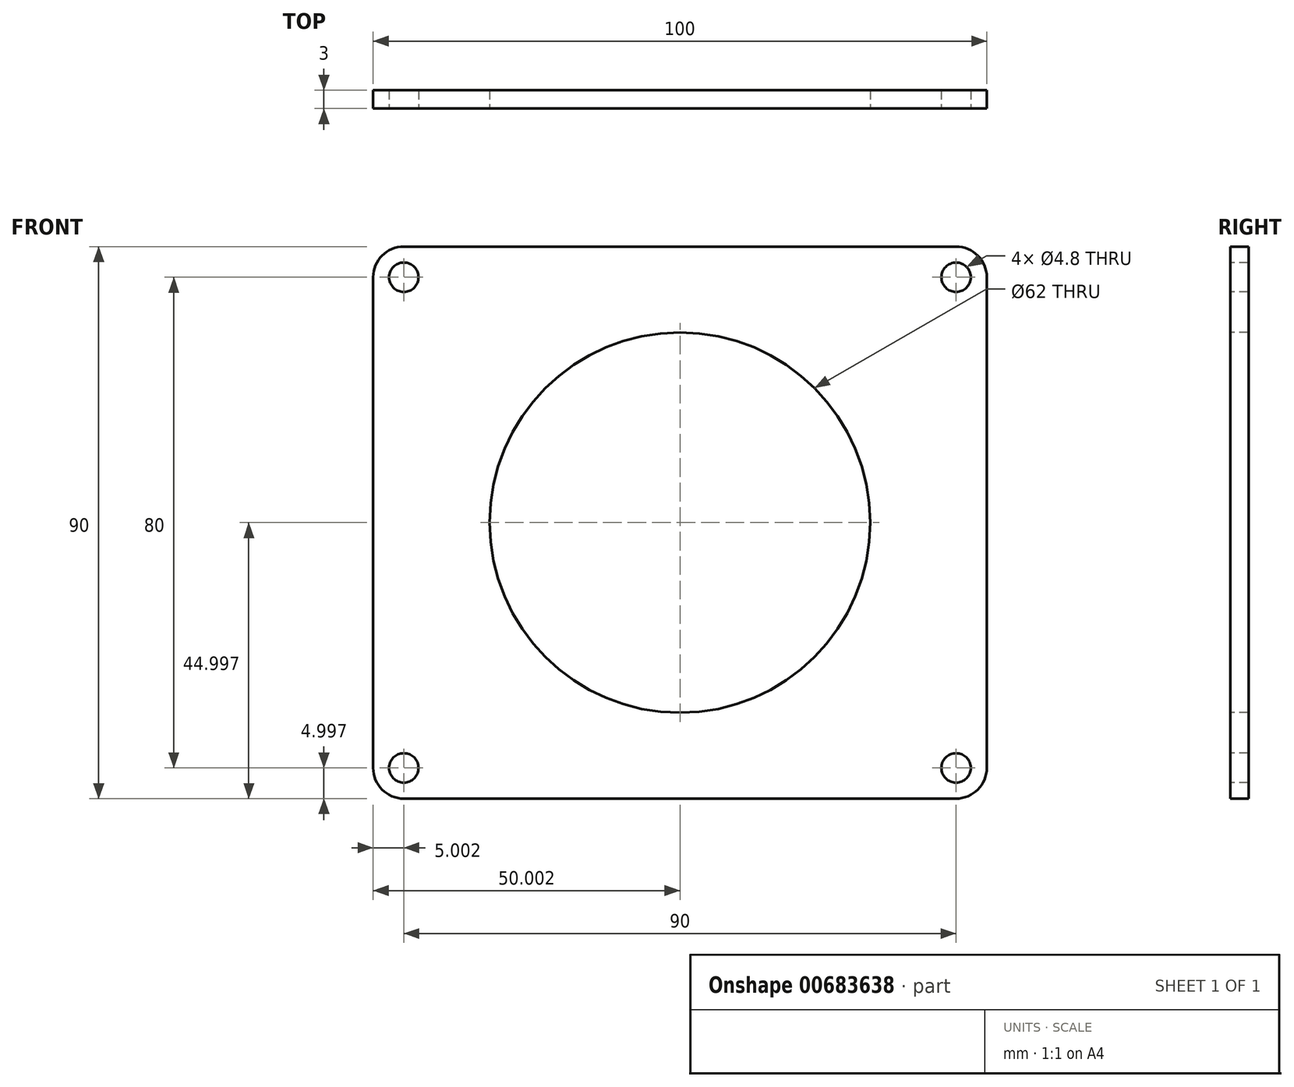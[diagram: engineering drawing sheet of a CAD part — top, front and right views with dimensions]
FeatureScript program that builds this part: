
annotation { "Feature Type Name" : "Feature", "Feature Type Description" : "" }
export const myFeature = defineFeature(function(context is Context, id is Id, definition is map)
    precondition{}
    {
        {
            var Q0;
            Q0=qCreatedBy(makeId("Front.planeOp"),FACE);
            var sketch = newSketch(context, id + "F0", { "sketchPlane" : qUnion([Q0])});
            skLineSegment(sketch, "E0.bottom", {"start": v(-1776.2, -1489.16) * mm, "end": v(-1676.2, -1489.16) * mm});
            skLineSegment(sketch, "E0.top", {"start": v(-1776.2, -1579.16) * mm, "end": v(-1676.2, -1579.16) * mm});
            skLineSegment(sketch, "E0.left", {"start": v(-1776.2, -1489.16) * mm, "end": v(-1776.2, -1579.16) * mm});
            skLineSegment(sketch, "E0.right", {"start": v(-1676.2, -1489.16) * mm, "end": v(-1676.2, -1579.16) * mm});
            skSolve(sketch);
        }
        {
            var Q0;
            Q0=qSketchRegion(id+"F0",true);
            extrude(context, id + "F1", {"entities" : qUnion([Q0]), "depth" : 3 * mm, "offsetDistance" : 25 * mm});
        }
        {
            var Q0;
            Q0=makeQuery(id+"F1.opExtrude","CAP_FACE",FACE,{"disambiguationData":[OSD([sQuery(id+"F0.wireOp",EDGE,"E0.bottom"),sQuery(id+"F0.wireOp",EDGE,"E0.top"),sQuery(id+"F0.wireOp",EDGE,"E0.left"),sQuery(id+"F0.wireOp",EDGE,"E0.right")])],"isStart":false});
            var sketch = newSketch(context, id + "F2", { "sketchPlane" : qUnion([Q0])});
            skPoint(sketch, "E1", {"position": v(-1771.2, -1494.16) * mm});
            skPoint(sketch, "E2", {"position": v(-1681.2, -1494.16) * mm});
            skPoint(sketch, "E3", {"position": v(-1681.2, -1574.16) * mm});
            skPoint(sketch, "E4", {"position": v(-1771.2, -1574.16) * mm});
            skSolve(sketch);
        }
        {
            var Q0;
            Q0=sQuery(id+"F2.wireOp",VERTEX,"E1");
            var Q1;
            Q1=sQuery(id+"F2.wireOp",VERTEX,"E2");
            var Q2;
            Q2=sQuery(id+"F2.wireOp",VERTEX,"E3");
            var Q3;
            Q3=sQuery(id+"F2.wireOp",VERTEX,"E4");
            var Q4;
            Q4=makeQuery(id+"F1.opExtrude","SWEPT_BODY",BODY,{"disambiguationData":[OSD([sQuery(id+"F0.wireOp",EDGE,"E0.bottom"),sQuery(id+"F0.wireOp",EDGE,"E0.top"),sQuery(id+"F0.wireOp",EDGE,"E0.left"),sQuery(id+"F0.wireOp",EDGE,"E0.right")])]});
            hole(context, id + "F3", {"style" : HoleStyle.SIMPLE, "endStyle" : HoleEndStyle.BLIND, "holeDiameter" : 4.8 * mm, "majorDiameter" : 5 * mm, "holeDepth" : 10 * mm, "isTappedThrough" : true, "tappedDepth" : 12 * mm, "tapClearance" : 3, "locations" : qUnion([Q0, Q1, Q2, Q3]), "scope" : qUnion([Q4])});
        }
        {
            var Q0;
            Q0=makeQuery(id+"F1.opExtrude","SWEPT_EDGE",EDGE,{"disambiguationData":[OSD([sQuery(id+"F0.wireOp",EDGE,"E0.bottom"),sQuery(id+"F0.wireOp",EDGE,"E0.right")])]});
            var Q1;
            Q1=makeQuery(id+"F1.opExtrude","SWEPT_EDGE",EDGE,{"disambiguationData":[OSD([sQuery(id+"F0.wireOp",EDGE,"E0.top"),sQuery(id+"F0.wireOp",EDGE,"E0.right")])]});
            var Q2;
            Q2=makeQuery(id+"F1.opExtrude","SWEPT_EDGE",EDGE,{"disambiguationData":[OSD([sQuery(id+"F0.wireOp",EDGE,"E0.bottom"),sQuery(id+"F0.wireOp",EDGE,"E0.left")])]});
            var Q3;
            Q3=makeQuery(id+"F1.opExtrude","SWEPT_EDGE",EDGE,{"disambiguationData":[OSD([sQuery(id+"F0.wireOp",EDGE,"E0.top"),sQuery(id+"F0.wireOp",EDGE,"E0.left")])]});
            fillet(context, id + "F4", {"entities" : qUnion([Q0, Q1, Q2, Q3]), "radius" : 5 * mm, "tangentPropagation" : true, "allowEdgeOverflow" : false});
        }
        {
            var Q0;
            Q0=makeQuery(id+"F1.opExtrude","CAP_FACE",FACE,{"disambiguationData":[OSD([sQuery(id+"F0.wireOp",EDGE,"E0.bottom"),sQuery(id+"F0.wireOp",EDGE,"E0.top"),sQuery(id+"F0.wireOp",EDGE,"E0.left"),sQuery(id+"F0.wireOp",EDGE,"E0.right")])],"isStart":false});
            var sketch = newSketch(context, id + "F5", { "sketchPlane" : qUnion([Q0])});
            skPoint(sketch, "E5", {"position": v(-1726.2, -1534.16) * mm});
            skSolve(sketch);
        }
        {
            var Q0;
            Q0=sQuery(id+"F5.wireOp",VERTEX,"E5");
            var Q1;
            Q1=makeQuery(id+"F1.opExtrude","SWEPT_BODY",BODY,{"disambiguationData":[OSD([sQuery(id+"F0.wireOp",EDGE,"E0.bottom"),sQuery(id+"F0.wireOp",EDGE,"E0.top"),sQuery(id+"F0.wireOp",EDGE,"E0.left"),sQuery(id+"F0.wireOp",EDGE,"E0.right")])]});
            hole(context, id + "F6", {"style" : HoleStyle.SIMPLE, "endStyle" : HoleEndStyle.BLIND, "holeDiameter" : 62 * mm, "majorDiameter" : 5 * mm, "holeDepth" : 10 * mm, "isTappedThrough" : true, "tappedDepth" : 12 * mm, "tapClearance" : 3, "locations" : qUnion([Q0]), "scope" : qUnion([Q1])});
        }
    });
